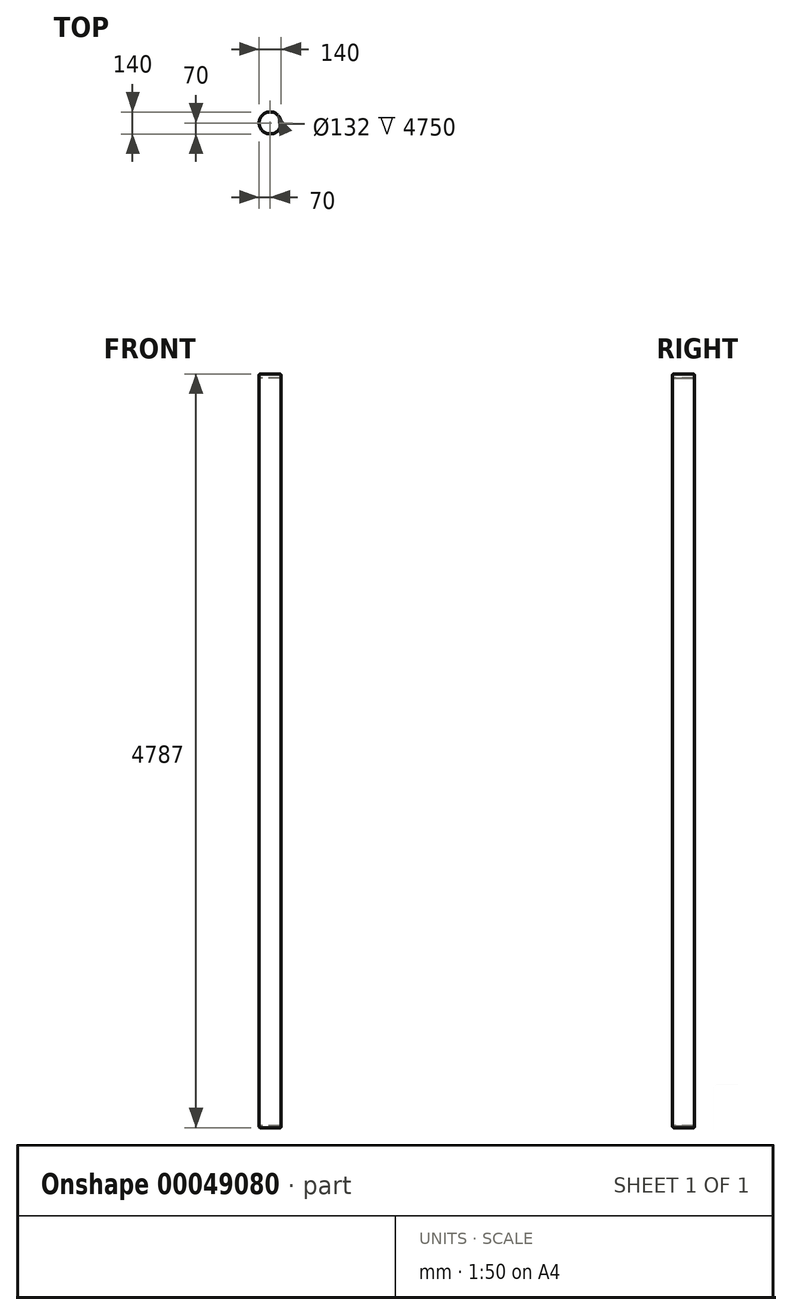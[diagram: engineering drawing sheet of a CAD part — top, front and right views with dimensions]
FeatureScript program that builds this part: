
annotation { "Feature Type Name" : "Feature", "Feature Type Description" : "" }
export const myFeature = defineFeature(function(context is Context, id is Id, definition is map)
    precondition{}
    {
        {
            var Q0;
            Q0=qCreatedBy(makeId("Top.planeOp"),FACE);
            var sketch = newSketch(context, id + "F0", { "sketchPlane" : qUnion([Q0])});
            skCircle(sketch, "E0", {"center": v(0, 0) * mm, "radius": 70 * mm});
            skCircle(sketch, "E1", {"center": v(0, 0) * mm, "radius": 66 * mm});
            skSolve(sketch);
        }
        {
            var Q0;
            Q0=makeQuery(id+"F0.imprint","IMPRINT",FACE,{"disambiguationData":[TD([[makeQuery(id+"F0.imprint","IMPRINT",EDGE,{"derivedFrom":sQuery(id+"F0.wireOp",EDGE,"E0")}),1.0]])]});
            extrude(context, id + "F1", {"entities" : qUnion([Q0]), "depth" : 4750 * mm});
        }
        {
            var Q0;
            Q0=qCreatedBy(makeId("Top.planeOp"),FACE);
            var sketch = newSketch(context, id + "F2", { "sketchPlane" : qUnion([Q0])});
            skCircle(sketch, "E2", {"center": v(0, 0) * mm, "radius": 70 * mm});
            skSolve(sketch);
        }
        {
            var Q0;
            Q0=makeQuery(id+"F2.imprint","IMPRINT",FACE,{"disambiguationData":[TD([[makeQuery(id+"F2.imprint","IMPRINT",EDGE,{"derivedFrom":sQuery(id+"F2.wireOp",EDGE,"E2")}),1.0]])]});
            extrude(context, id + "F3", {"entities" : qUnion([Q0]), "operationType" : NewBodyOperationType.ADD, "oppositeDirection" : true, "depth" : 12 * mm});
        }
        {
            var Q0;
            Q0=makeQuery(id+"F3.opExtrude","CAP_EDGE",EDGE,{"disambiguationData":[OSD([sQuery(id+"F2.wireOp",EDGE,"E2")])],"isStart":false});
            fillet(context, id + "F4", {"entities" : qUnion([Q0]), "radius" : 8 * mm, "tangentPropagation" : true, "allowEdgeOverflow" : false});
        }
        {
            var Q0;
            Q0=makeQuery(id+"F1.opExtrude","CAP_FACE",FACE,{"disambiguationData":[OSD([sQuery(id+"F0.wireOp",EDGE,"E0"),sQuery(id+"F0.wireOp",EDGE,"E1")])],"isStart":false});
            var sketch = newSketch(context, id + "F5", { "sketchPlane" : qUnion([Q0])});
            skCircle(sketch, "E3", {"center": v(0, 0) * mm, "radius": 70.1 * mm});
            skSolve(sketch);
        }
        {
            var Q0;
            Q0=makeQuery(id+"F5.imprint","IMPRINT",FACE,{"disambiguationData":[TD([[makeQuery(id+"F5.imprint","IMPRINT",EDGE,{"derivedFrom":makeQuery(id+"F1.opExtrude","CAP_EDGE",EDGE,{"disambiguationData":[OSD([sQuery(id+"F0.wireOp",EDGE,"E1")])],"isStart":false})}),1.0]])]});
            var Q1;
            Q1=makeQuery(id+"F5.imprint","IMPRINT",FACE,{"disambiguationData":[TD([[makeQuery(id+"F5.imprint","IMPRINT",EDGE,{"derivedFrom":makeQuery(id+"F1.opExtrude","CAP_EDGE",EDGE,{"disambiguationData":[OSD([sQuery(id+"F0.wireOp",EDGE,"E0")])],"isStart":false})}),1.0]])]});
            extrude(context, id + "F6", {"entities" : qUnion([Q0, Q1]), "operationType" : NewBodyOperationType.ADD, "depth" : 25 * mm});
        }
        {
            var Q0;
            Q0=makeQuery(id+"F6.opExtrude","CAP_EDGE",EDGE,{"disambiguationData":[OSD([sQuery(id+"F0.wireOp",EDGE,"E0")])],"isStart":false});
            fillet(context, id + "F7", {"entities" : qUnion([Q0]), "radius" : 8 * mm, "tangentPropagation" : true, "allowEdgeOverflow" : false});
        }
    });
